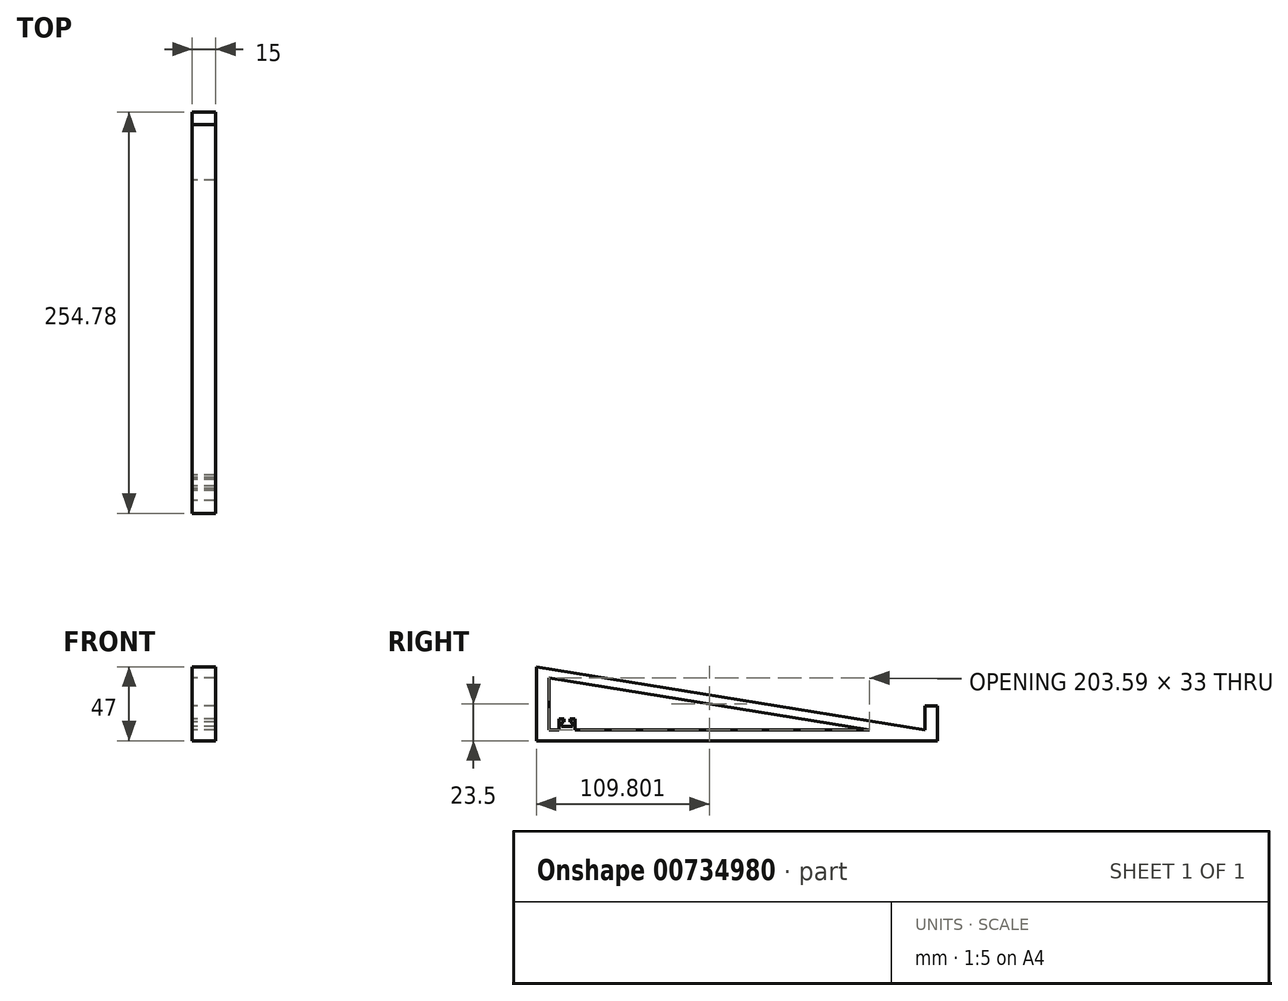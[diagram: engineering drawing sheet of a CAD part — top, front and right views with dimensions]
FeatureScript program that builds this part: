
annotation { "Feature Type Name" : "Feature", "Feature Type Description" : "" }
export const myFeature = defineFeature(function(context is Context, id is Id, definition is map)
    precondition{}
    {
        {
            var Q0;
            Q0=qCreatedBy(makeId("Right.planeOp"),FACE);
            var sketch = newSketch(context, id + "F0", { "sketchPlane" : qUnion([Q0])});
            skLineSegment(sketch, "E0", {"start": v(117.13, 0) * mm, "end": v(117.13, 22) * mm});
            skLineSegment(sketch, "E1", {"start": v(117.13, 22) * mm, "end": v(109.13, 22) * mm});
            skLineSegment(sketch, "E2", {"start": v(109.13, 22) * mm, "end": v(109.13, 7) * mm});
            skLineSegment(sketch, "E3", {"start": v(109.13, 7) * mm, "end": v(-137.65, 47) * mm});
            skLineSegment(sketch, "E4", {"start": v(-137.65, 47) * mm, "end": v(-137.65, 0) * mm});
            skLineSegment(sketch, "E5", {"start": v(-137.65, 0) * mm, "end": v(-129.65, 0) * mm});
            skLineSegment(sketch, "E6", {"start": v(-129.65, 0) * mm, "end": v(-129.65, 40) * mm});
            skLineSegment(sketch, "E7", {"start": v(-129.65, 40) * mm, "end": v(117.13, 0) * mm});
            skLineSegment(sketch, "E8", {"start": v(-129.65, 0) * mm, "end": v(117.13, 0) * mm});
            skLineSegment(sketch, "E9", {"start": v(-129.65, 7) * mm, "end": v(109.13, 7) * mm});
            skLineSegment(sketch, "E10", {"start": v(-123.3, 7) * mm, "end": v(-123.3, 14) * mm});
            skLineSegment(sketch, "E11", {"start": v(-123.3, 14) * mm, "end": v(-120.3, 14) * mm});
            skLineSegment(sketch, "E12", {"start": v(-120.3, 14) * mm, "end": v(-120.3, 12) * mm});
            skLineSegment(sketch, "E13", {"start": v(-120.3, 12) * mm, "end": v(-121.8, 12) * mm});
            skLineSegment(sketch, "E14", {"start": v(-121.8, 12) * mm, "end": v(-121.8, 9) * mm});
            skLineSegment(sketch, "E15", {"start": v(-121.8, 9) * mm, "end": v(-114.8, 9) * mm});
            skLineSegment(sketch, "E16", {"start": v(-114.8, 9) * mm, "end": v(-114.8, 12) * mm});
            skLineSegment(sketch, "E17", {"start": v(-114.8, 12) * mm, "end": v(-116.3, 12) * mm});
            skLineSegment(sketch, "E18", {"start": v(-116.3, 12) * mm, "end": v(-116.3, 14) * mm});
            skLineSegment(sketch, "E19", {"start": v(-116.3, 14) * mm, "end": v(-113.3, 14) * mm});
            skLineSegment(sketch, "E20", {"start": v(-113.3, 14) * mm, "end": v(-113.3, 7) * mm});
            skLineSegment(sketch, "E21", {"start": v(-113.3, 7) * mm, "end": v(-113.3, 14) * mm});
            skLineSegment(sketch, "E22", {"start": v(-113.3, 14) * mm, "end": v(-110.3, 14) * mm});
            skLineSegment(sketch, "E23", {"start": v(-110.3, 14) * mm, "end": v(-110.3, 12) * mm});
            skLineSegment(sketch, "E24", {"start": v(-110.3, 12) * mm, "end": v(-111.8, 12) * mm});
            skLineSegment(sketch, "E25", {"start": v(-111.8, 12) * mm, "end": v(-111.8, 9) * mm});
            skLineSegment(sketch, "E26", {"start": v(-111.8, 9) * mm, "end": v(-104.8, 9) * mm});
            skLineSegment(sketch, "E27", {"start": v(-104.8, 9) * mm, "end": v(-104.8, 12) * mm});
            skLineSegment(sketch, "E28", {"start": v(-104.8, 12) * mm, "end": v(-106.3, 12) * mm});
            skLineSegment(sketch, "E29", {"start": v(-106.3, 12) * mm, "end": v(-106.3, 14) * mm});
            skLineSegment(sketch, "E30", {"start": v(-106.3, 14) * mm, "end": v(-103.3, 14) * mm});
            skLineSegment(sketch, "E31", {"start": v(-103.3, 14) * mm, "end": v(-103.3, 7) * mm});
            skLineSegment(sketch, "E32", {"start": v(-103.3, 7) * mm, "end": v(-103.3, 14) * mm});
            skLineSegment(sketch, "E33", {"start": v(-103.3, 14) * mm, "end": v(-100.3, 14) * mm});
            skLineSegment(sketch, "E34", {"start": v(-100.3, 14) * mm, "end": v(-100.3, 12) * mm});
            skLineSegment(sketch, "E35", {"start": v(-100.3, 12) * mm, "end": v(-101.8, 12) * mm});
            skLineSegment(sketch, "E36", {"start": v(-101.8, 12) * mm, "end": v(-101.8, 9) * mm});
            skLineSegment(sketch, "E37", {"start": v(-101.8, 9) * mm, "end": v(-94.8, 9) * mm});
            skLineSegment(sketch, "E38", {"start": v(-94.8, 9) * mm, "end": v(-94.8, 12) * mm});
            skLineSegment(sketch, "E39", {"start": v(-94.8, 12) * mm, "end": v(-96.3, 12) * mm});
            skLineSegment(sketch, "E40", {"start": v(-96.3, 12) * mm, "end": v(-96.3, 14) * mm});
            skLineSegment(sketch, "E41", {"start": v(-96.3, 14) * mm, "end": v(-93.3, 14) * mm});
            skLineSegment(sketch, "E42", {"start": v(-93.3, 14) * mm, "end": v(-93.3, 7) * mm});
            skSolve(sketch);
        }
        {
            var Q0;
            Q0=qSketchRegion(id+"F0",true);
            var Q1;
            {var subQ0=sQuery(id+"F0.wireOp",EDGE,"E10");Q1=makeQuery(id+"F0.imprint","IMPRINT",FACE,{"disambiguationData":[TD([[makeQuery(id+"F0.imprint","IMPRINT",EDGE,{"derivedFrom":subQ0}),-1.0]])]});}
            var Q2;
            {var subQ0=sQuery(id+"F0.wireOp",EDGE,"E21");Q2=makeQuery(id+"F0.imprint","IMPRINT",FACE,{"disambiguationData":[TD([[makeQuery(id+"F0.imprint","IMPRINT",EDGE,{"derivedFrom":subQ0}),-1.0]])]});}
            var Q3;
            {var subQ0=sQuery(id+"F0.wireOp",EDGE,"E32");Q3=makeQuery(id+"F0.imprint","IMPRINT",FACE,{"disambiguationData":[TD([[makeQuery(id+"F0.imprint","IMPRINT",EDGE,{"derivedFrom":subQ0}),-1.0]])]});}
            extrude(context, id + "F1", {"entities" : qUnion([Q0, Q1, Q2, Q3]), "depth" : 15 * mm, "offsetDistance" : 25 * mm});
        }
    });
